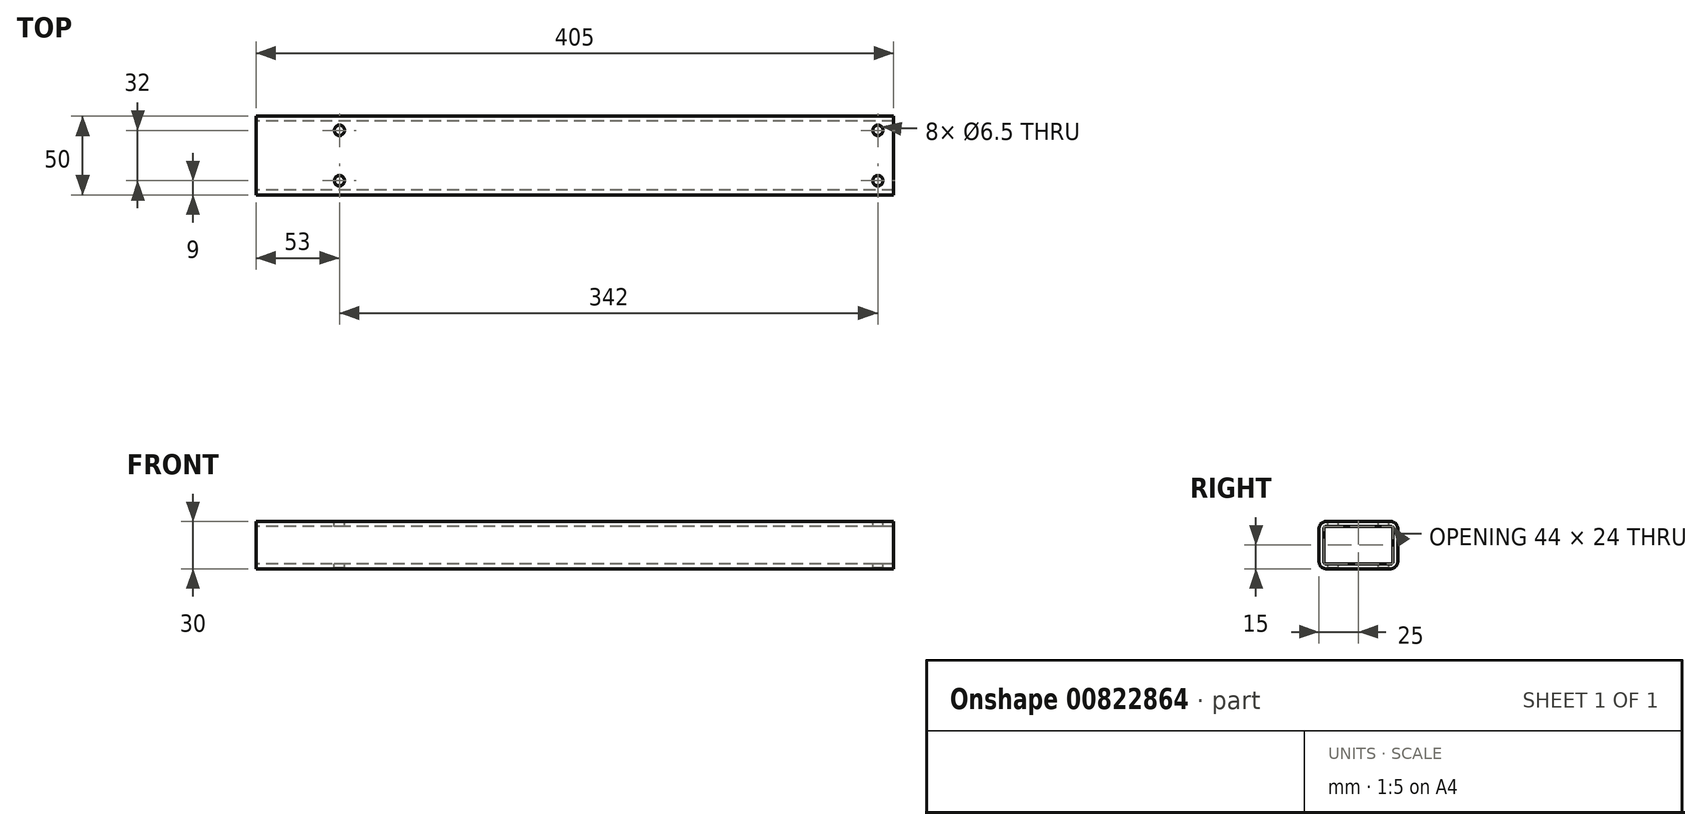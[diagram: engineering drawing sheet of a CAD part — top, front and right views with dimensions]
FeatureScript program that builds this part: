
annotation { "Feature Type Name" : "Feature", "Feature Type Description" : "" }
export const myFeature = defineFeature(function(context is Context, id is Id, definition is map)
    precondition{}
    {
        {
            var Q0;
            Q0=qCreatedBy(makeId("Right.planeOp"),FACE);
            var sketch = newSketch(context, id + "F0", { "sketchPlane" : qUnion([Q0])});
            skLineSegment(sketch, "E0.bottom", {"start": v(-25, -15) * mm, "end": v(25, -15) * mm});
            skLineSegment(sketch, "E0.top", {"start": v(-25, 15) * mm, "end": v(25, 15) * mm});
            skLineSegment(sketch, "E0.left", {"start": v(-25, -15) * mm, "end": v(-25, 15) * mm});
            skLineSegment(sketch, "E0.right", {"start": v(25, -15) * mm, "end": v(25, 15) * mm});
            skPoint(sketch, "E0.middle", {"position": v(0, 0) * mm});
            skLineSegment(sketch, "E1.0", {"start": v(-22, 12) * mm, "end": v(22, 12) * mm});
            skLineSegment(sketch, "E1.1", {"start": v(-22, -12) * mm, "end": v(-22, 12) * mm});
            skLineSegment(sketch, "E1.2", {"start": v(-22, -12) * mm, "end": v(22, -12) * mm});
            skLineSegment(sketch, "E1.3", {"start": v(22, -12) * mm, "end": v(22, 12) * mm});
            skSolve(sketch);
        }
        {
            var Q0;
            Q0=qSketchRegion(id+"F0",true);
            extrude(context, id + "F1", {"entities" : qUnion([Q0]), "endBound" : BoundingType.SYMMETRIC, "depth" : 362 * mm, "offsetDistance" : 25 * mm});
        }
        {
            var Q0;
            Q0=makeQuery(id+"F1.opExtrude","SWEPT_EDGE",EDGE,{"disambiguationData":[OSD([sQuery(id+"F0.wireOp",EDGE,"E1.1"),sQuery(id+"F0.wireOp",EDGE,"E1.2")])]});
            var Q1;
            Q1=makeQuery(id+"F1.opExtrude","SWEPT_EDGE",EDGE,{"disambiguationData":[OSD([sQuery(id+"F0.wireOp",EDGE,"E1.0"),sQuery(id+"F0.wireOp",EDGE,"E1.1")])]});
            var Q2;
            Q2=makeQuery(id+"F1.opExtrude","SWEPT_EDGE",EDGE,{"disambiguationData":[OSD([sQuery(id+"F0.wireOp",EDGE,"E1.2"),sQuery(id+"F0.wireOp",EDGE,"E1.3")])]});
            var Q3;
            Q3=makeQuery(id+"F1.opExtrude","SWEPT_EDGE",EDGE,{"disambiguationData":[OSD([sQuery(id+"F0.wireOp",EDGE,"E1.0"),sQuery(id+"F0.wireOp",EDGE,"E1.3")])]});
            fillet(context, id + "F2", {"entities" : qUnion([Q0, Q1, Q2, Q3]), "radius" : 1.5 * mm, "tangentPropagation" : true, "allowEdgeOverflow" : false});
        }
        {
            var Q0;
            Q0=makeQuery(id+"F1.opExtrude","SWEPT_EDGE",EDGE,{"disambiguationData":[OSD([sQuery(id+"F0.wireOp",EDGE,"E0.top"),sQuery(id+"F0.wireOp",EDGE,"E0.left")])]});
            var Q1;
            Q1=makeQuery(id+"F1.opExtrude","SWEPT_EDGE",EDGE,{"disambiguationData":[OSD([sQuery(id+"F0.wireOp",EDGE,"E0.bottom"),sQuery(id+"F0.wireOp",EDGE,"E0.left")])]});
            var Q2;
            Q2=makeQuery(id+"F1.opExtrude","SWEPT_EDGE",EDGE,{"disambiguationData":[OSD([sQuery(id+"F0.wireOp",EDGE,"E0.bottom"),sQuery(id+"F0.wireOp",EDGE,"E0.right")])]});
            var Q3;
            Q3=makeQuery(id+"F1.opExtrude","SWEPT_EDGE",EDGE,{"disambiguationData":[OSD([sQuery(id+"F0.wireOp",EDGE,"E0.top"),sQuery(id+"F0.wireOp",EDGE,"E0.right")])]});
            fillet(context, id + "F3", {"entities" : qUnion([Q0, Q1, Q2, Q3]), "radius" : 4.5 * mm, "tangentPropagation" : true, "allowEdgeOverflow" : false});
        }
        {
            var Q0;
            Q0=makeQuery(id+"F1.opExtrude","SWEPT_FACE",FACE,{"disambiguationData":[OSD([sQuery(id+"F0.wireOp",EDGE,"E0.top")])]});
            var sketch = newSketch(context, id + "F4", { "sketchPlane" : qUnion([Q0])});
            skLineSegment(sketch, "E2.bottom", {"start": v(-171, 16) * mm, "end": v(171, 16) * mm, "construction": true});
            skLineSegment(sketch, "E2.top", {"start": v(-171, -16) * mm, "end": v(171, -16) * mm, "construction": true});
            skLineSegment(sketch, "E2.left", {"start": v(-171, 16) * mm, "end": v(-171, -16) * mm, "construction": true});
            skLineSegment(sketch, "E2.right", {"start": v(171, 16) * mm, "end": v(171, -16) * mm, "construction": true});
            skPoint(sketch, "E2.middle", {"position": v(0, 0) * mm});
            skCircle(sketch, "E3", {"center": v(-171, 16) * mm, "radius": 3.25 * mm});
            skCircle(sketch, "E4", {"center": v(-171, -16) * mm, "radius": 3.25 * mm});
            skCircle(sketch, "E5", {"center": v(171, -16) * mm, "radius": 3.25 * mm});
            skCircle(sketch, "E6", {"center": v(171, 16) * mm, "radius": 3.25 * mm});
            skSolve(sketch);
        }
        {
            var Q0;
            Q0=qSketchRegion(id+"F4",true);
            extrude(context, id + "F5", {"entities" : qUnion([Q0]), "operationType" : NewBodyOperationType.REMOVE, "oppositeDirection" : true, "depth" : 35 * mm, "offsetDistance" : 25 * mm});
        }
        {
            var Q0;
            Q0=makeQuery(id+"F5.boolean.opBoolean","COPY",EDGE,{"derivedFrom":makeQuery(id+"F5.opExtrude","CAP_EDGE",EDGE,{"disambiguationData":[OSD([sQuery(id+"F4.wireOp",EDGE,"E4")])],"isStart":true})});
            var Q1;
            Q1=makeQuery(id+"F5.boolean.opBoolean","COPY",EDGE,{"derivedFrom":makeQuery(id+"F5.opExtrude","CAP_EDGE",EDGE,{"disambiguationData":[OSD([sQuery(id+"F4.wireOp",EDGE,"E3")])],"isStart":true})});
            var Q2;
            Q2=makeQuery(id+"F5.boolean.opBoolean","COPY",EDGE,{"derivedFrom":makeQuery(id+"F5.opExtrude","CAP_EDGE",EDGE,{"disambiguationData":[OSD([sQuery(id+"F4.wireOp",EDGE,"E5")])],"isStart":true})});
            var Q3;
            Q3=makeQuery(id+"F5.boolean.opBoolean","COPY",EDGE,{"derivedFrom":makeQuery(id+"F5.opExtrude","CAP_EDGE",EDGE,{"disambiguationData":[OSD([sQuery(id+"F4.wireOp",EDGE,"E6")])],"isStart":true})});
            var Q4;
            Q4=makeQuery(id+"F5.boolean.opBoolean","INTERSECT",EDGE,{"derivedFrom":[makeQuery(id+"F1.opExtrude","SWEPT_FACE",FACE,{"disambiguationData":[OSD([sQuery(id+"F0.wireOp",EDGE,"E0.bottom")])]}),makeQuery(id+"F5.opExtrude","SWEPT_FACE",FACE,{"disambiguationData":[OSD([sQuery(id+"F4.wireOp",EDGE,"E6")])]})]});
            var Q5;
            Q5=makeQuery(id+"F5.boolean.opBoolean","INTERSECT",EDGE,{"derivedFrom":[makeQuery(id+"F1.opExtrude","SWEPT_FACE",FACE,{"disambiguationData":[OSD([sQuery(id+"F0.wireOp",EDGE,"E0.bottom")])]}),makeQuery(id+"F5.opExtrude","SWEPT_FACE",FACE,{"disambiguationData":[OSD([sQuery(id+"F4.wireOp",EDGE,"E5")])]})]});
            var Q6;
            Q6=makeQuery(id+"F5.boolean.opBoolean","INTERSECT",EDGE,{"derivedFrom":[makeQuery(id+"F1.opExtrude","SWEPT_FACE",FACE,{"disambiguationData":[OSD([sQuery(id+"F0.wireOp",EDGE,"E0.bottom")])]}),makeQuery(id+"F5.opExtrude","SWEPT_FACE",FACE,{"disambiguationData":[OSD([sQuery(id+"F4.wireOp",EDGE,"E3")])]})]});
            var Q7;
            Q7=makeQuery(id+"F5.boolean.opBoolean","INTERSECT",EDGE,{"derivedFrom":[makeQuery(id+"F1.opExtrude","SWEPT_FACE",FACE,{"disambiguationData":[OSD([sQuery(id+"F0.wireOp",EDGE,"E0.bottom")])]}),makeQuery(id+"F5.opExtrude","SWEPT_FACE",FACE,{"disambiguationData":[OSD([sQuery(id+"F4.wireOp",EDGE,"E4")])]})]});
            chamfer(context, id + "F6", {"entities" : qUnion([Q0, Q1, Q2, Q3, Q4, Q5, Q6, Q7]), "width" : 0.5 * mm, "tangentPropagation" : true});
        }
        {
            var Q0;
            Q0=makeQuery(id+"F1.opExtrude","CAP_FACE",FACE,{"disambiguationData":[OSD([sQuery(id+"F0.wireOp",EDGE,"E0.bottom"),sQuery(id+"F0.wireOp",EDGE,"E0.top"),sQuery(id+"F0.wireOp",EDGE,"E0.left"),sQuery(id+"F0.wireOp",EDGE,"E0.right"),sQuery(id+"F0.wireOp",EDGE,"E1.0"),sQuery(id+"F0.wireOp",EDGE,"E1.1"),sQuery(id+"F0.wireOp",EDGE,"E1.2"),sQuery(id+"F0.wireOp",EDGE,"E1.3")])],"isStart":true});
            extrude(context, id + "F7", {"entities" : qUnion([Q0]), "operationType" : NewBodyOperationType.ADD, "depth" : (400 - 362 + 5) * mm, "offsetDistance" : 25 * mm});
        }
    });
